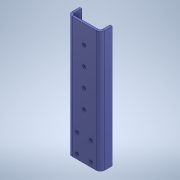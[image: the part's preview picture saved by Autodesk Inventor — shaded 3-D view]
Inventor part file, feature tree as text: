
AUTODESK INVENTOR PART (.ipt)
format: ipt  version: 2022 (Build 260153000, 153)  size: 125,952 bytes
history: imported  units: in
note: dims shown in document units (in); Inventor stores cm internally (conversion verified against a paired STEP export)
features: imported_body x1
ambient origin geometry x8: Origin, YZ Plane, XZ Plane, XY Plane, X Axis, Y Axis, Z Axis, Center Point
bodies: Solid1 (imported_parasolid), Body2 (imported_parasolid)
feature tree (1):
  imported_body  NMx_Import_Brep_tag  [imported B-rep: ~30 faces, bbox_mm=[35.0, 130.0, 12.7]]
